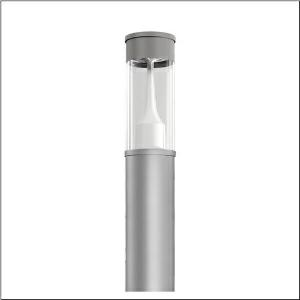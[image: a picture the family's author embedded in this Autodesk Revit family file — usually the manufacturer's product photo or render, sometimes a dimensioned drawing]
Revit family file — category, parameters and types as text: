
# Revit family: city-light_400_iq___st1_2a_5xa5305ef14hp_9457
name_source: partatom
category: Lighting Fixtures
units: mm (PartAtom-declared; Revit-internal decimal feet)

## family parameters
Cut with Voids When Loaded = No
Host = Face
Light Source = No
Part Type = Normal
Room Calculation Point = No
Round Connector Dimension = Use Diameter
Shared = No

## types (1)
- --- (1 x LED, 4730 lm, 33.6 W, 3000K)
    Apparent Load = 34 VA
    CIE Flux Codes = 22 61 94 96 100
    Color Rendering = 70
    Color Temperature = 3000K
    Default Elevation = 1800 mm
    Description = City-Light 400 iQ, light pillar, Module 540 iQ-SR, primary light control with 3 zone facetted reflector, of plastic, silver coated, highly specular, structured, primary optical cover: cover, of PMMA, transparent, partly coated, light distribution: ST1.2a, primary light characteristic: asymmetric, LED, High Power LED, rated luminous flux: 4.730lm, luminous efficacy: 141lm/W, light colour: 730, colour temperature: 3000K, control gear: ECG iQ, control: presetting dimming logarithmic, Street-Remote, Auto-Match, Temp-Guard, Lumen-Switch, Night-Set, Smart-Wire, Light-Fading, Desk-Remote (wireless, voltage-free reading and setting of iQ features in the workshop via application-optimized NFC function/RFID function), optimised constant luminous flux control (CLO 2.0), with terminal, 6-pole, max. 2.5mm², mains connection: 230..240V, AC, 50/60Hz, start of lifetime: 34W, end of service life: 36W, reduction: 15W, luminaire housing, cylindrical, of extruded aluminium section, coated, Siteco® metallic grey (DB 702S), length: 4.694mm, diameter: 200mm, Module 540 iQ-SR, traffic white (RAL 9016), equipment: Power, protection rating (complete): IP65, insulation class (complete): insulation class II (safety insulation), certification: CE, ENEC, VDE, packaging unit: 1 piece

Light Distribution: ST1.2a
    Height = 500 mm
    Lamp = 1 x LED
    Lamp Light Flux = 4730 lm
    Lamp Power = 33.6 W
    Lamp count = 1
    Length = 200 mm  [stored 0.656168 ft]
    Luminous efficacy = 141 lm/W
    Manufacturer = Siteco
    ModVariant = No
    Model = 5XA5305EF14HP
    Mounting Place = Floor
    Mounting Type = Freestanding
    Number of Poles = 1
    OnlyDefault = Yes
    Power Factor = 1
    Product Name = City-Light 400 iQ | ST1.2a
    Product group = light pillar
    ProductGroupID = 1303
    Protection Class = Protection class II
    Protection Degree = IP 65
    RLX_Detail_Level = 1
    RLX_Emergency_Light_Flux = 0 lm
    RLX_Emergency_Type = 0
    RLX_Emergency_Type_DB = No
    RlxData = <blob elided: 53589 chars, md5=0dd56d5f>
    Socket = socket
    Standby Power = 0 W
    System Light Flux = 4730 lm
    System Power = 34 W
    Type Comments = factory setting: luminous flux: 100 % | dim-lin: 254 | 695 mA
    Type Image = l_1006916.jpg
    URL = http://relux.com
    VarID = @adj_127297
    Voltage = 0 V
    Weight = 0.00 kg
    Width = 0 mm  [stored 0 ft]

note: [stored X ft] marks values corroborated as IEEE doubles in the binary element streams (Revit-internal decimal feet)

## geometry (parser evidence)
native form markers: Blend x4, Sweep x11
no freeform markers — native parametric forms only
